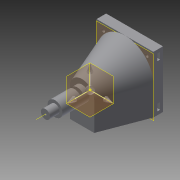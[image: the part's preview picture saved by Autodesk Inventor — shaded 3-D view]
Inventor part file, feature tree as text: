
AUTODESK INVENTOR PART (.ipt)
format: ipt  version: 2015 (Build 190159000, 159)  size: 239,616 bytes
history: native  units: in
note: dims shown in document units (in); Inventor stores cm internally (conversion verified against a paired STEP export)
features: sketch x10, extrude x9, other x4, mirror x1, plane x1, loft x1, revolve x1
ambient origin geometry x8: Origin, YZ Plane, XZ Plane, XY Plane, X Axis, Y Axis, Z Axis, Center Point
bodies: Solid1 (feature_tree)
feature tree (27):
  other  "Curvature1"
  extrude  "Extrusion1"  Depth=2.1654in TaperAngle=0.0deg
  extrude  "Extrusion2"  Depth=0.0787in
  extrude  "Extrusion3"  Depth=1.1142in
  sketch  "Sketch10"  dims[d24=0.2756in d25=0.1181in]
  extrude  "Extrusion5"  Depth=0.1181in
  extrude  "Extrusion4"  Depth=0.1969in
  mirror  "Mirror1"
  plane  "Work Plane1"
  extrude  "Extrusion6"  Depth=0.1181in
  loft  "Loft2"
  extrude  "Extrusion7"  Depth=0.2756in
  extrude  "Extrusion8"  Depth=0.1378in
  other  "Work Axis1"
  revolve  "Revolution1"  [1 undecoded]
  extrude  "Extrusion10"  TaperAngle=0.0deg  [1 undecoded]
  sketch  "Sketch2"  dims[d0=2.3425in d1=2.1654in d2=0.0in]
  sketch  "Sketch3"  dims[d3=0.6102in d5=0.0787in]
  sketch  "Sketch4"  dims[d6=1.1142in d7=0.0in d8=0.374in]
  sketch  "Sketch7"  dims[d9=0.3937in d10=0.0in d16=0.1181in]
  sketch  "Sketch9"  dims[d17=0.4724in d18=0.1969in]
  sketch  "Sketch11"  dims[d26=0.1181in d27=0.3937in d28=0.0in]
  other  "Edges2"
  other  "Edges3"
  sketch  "Sketch12"  dims[d29=0.2756in d30=0.2756in]
  sketch  "Sketch15"  dims[d34=0.3937in d36=0.0in d37=0.0in d38=0.0in d39=90.0deg d40=0.0in d41=90.0deg d42=1.2598in d43=0.0in d44=0.2362in d45=0.0in d46=0.0in d47=0.8661in d49=0.1969in d54=0.1969in d55=0.7874in d56=180.0deg d57=1.0in d58=0.0in]
  sketch  "Sketch14"  dims[d31=0.3937in d32=0.0in d33=0.1378in]
note: 2 required parameter values undecoded (feature->parameter linkage not recoverable at this tier; creation-order binding heuristic only, values carry confidence <= 0.55)